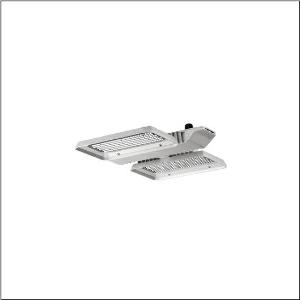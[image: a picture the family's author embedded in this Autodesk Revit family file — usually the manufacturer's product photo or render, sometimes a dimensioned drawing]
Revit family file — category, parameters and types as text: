
# Revit family: highbay_11_51hlasd14fga
name_source: partatom
category: Lighting Fixtures
units: mm (PartAtom-declared; Revit-internal decimal feet)

## family parameters
Cut with Voids When Loaded = No
Host = Face
Light Source = No
Part Type = Normal
Room Calculation Point = No
Round Connector Dimension = Use Diameter
Shared = No

## types (1)
- --- (1 x LED, 14400 lm, 81.3 W, 4000K)
    Apparent Load = 81 VA
    CIE Flux Codes = 89 96 99 100 100
    Color Rendering = 80
    Color Temperature = 4000K
    Default Elevation = 1800 mm
    Description = Highbay 11, LED high bay luminaire, primary light control with lens, of PMMA, light emission: direct distribution, primary light characteristic: symmetric, installation type: suspended mounting, for 1x 2x LED, rated luminous flux: 14.400lm, luminous efficacy: 177lm/W, light colour: 840, colour temperature: 4000K, control gear: ECG DALI, with terminal, 5-pole, max. 2.5mm², mains connection: 230..240V, AC, 50/60Hz, rated input power: 81W, LED unit, of diecast aluminium, unplated, bead blasted, silver, length: 470mm, width: 500mm, height: 65mm, housing, of diecast aluminium, uncoated, bead blasted, silver, protection rating (complete): IP20, insulation class (complete): insulation class I (protective earthing), certification: CE, ENEC, VDE, UKCA, protection symbol: D, ball protection: ball impact resistant according to DIN VDE 0710 part 13 (with chain suspension), permissible operating ambient temperature: -35..+55°C, corresponds to IFS (International Featured Standards) requirements for safety and quality in the food industry, reducing of maximum allowable ambient temperature of 5°C with ceiling mounting, packaging unit: 1 piece
    Height = 95 mm
    Lamp = 1 x LED
    Lamp Light Flux = 14400 lm
    Lamp Power = 81.3 W
    Lamp count = 1
    Length = 468 mm
    Luminous efficacy = 177 lm/W
    Manufacturer = Siteco
    ModVariant = No
    Model = 51HLASD14FGA
    Mounting Place = Ceiling
    Mounting Type = Pendant
    Number of Poles = 1
    OnlyDefault = Yes
    Power Factor = 1
    Product Name = Highbay 11
    Product group = LED high bay luminaire
    ProductGroupID = 903
    Protection Class = Protection class I
    Protection Degree = IP 20
    RLX_Detail_Level = 1
    RLX_Emergency_Light_Flux = 0 lm
    RLX_Emergency_Type = 0
    RLX_Emergency_Type_DB = No
    RlxData = <blob elided: 53425 chars, md5=eebf8bce>
    Socket = socket
    Standby Power = 0 W
    System Light Flux = 14400 lm
    System Power = 81 W
    Type Comments = factory setting: luminous flux: 100 % | dim-lin: 254 | 460 mA
    Type Image = l_1006019.jpg
    URL = http://relux.com
    VarID = @adj_143331
    Voltage = 0 V
    Weight = 0.00 kg
    Width = 501 mm

## geometry (parser evidence)
native form markers: Blend x4, Sweep x11
no freeform markers — native parametric forms only
